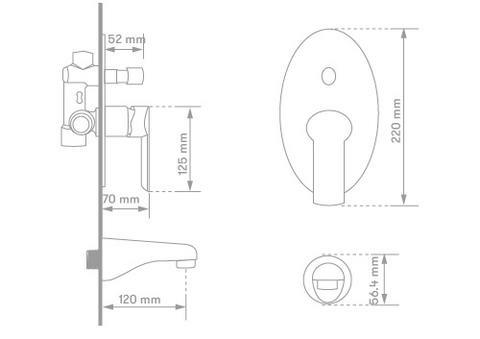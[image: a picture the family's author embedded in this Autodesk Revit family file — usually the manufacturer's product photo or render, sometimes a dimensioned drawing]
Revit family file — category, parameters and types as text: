
# Revit family: 01-3300-11SR-DUCHA KURVEN CON DESVIADOR SIN REGADERA
name_source: partatom
category: Aparatos sanitarios
revit_build: Autodesk Revit 2018 (Build: 20170223_1515(x64)
units: mm (PartAtom-declared; Revit-internal decimal feet)

## family parameters
Anfitrión = Cara
Compartido = No
Corte con vacíos al cargar = No
Cota de conector redondo = Diámetro de uso
Número OmniClass = 23.31.11.00
Punto de cálculo de habitación = No
Tipo de pieza = Normal

## types (1)
- 01-3300-11SR
    Alto = 220 mm  [stored 0.721785 ft]
    Ancho = 130 mm
    Conexión AC = Sí
    Conexión AF = Sí
    Conexión de residuos = No
    Conexión de ventilación = No
    Descripción = DUCHA MONOMANDO
    Elevación por defecto = 0 mm  [stored 0 ft]
    Fabricante = Gricol
    Finish = <Por categoría>
    Imagen de tipo = <Ninguno>
    Largo = 120 mm
    Link Ficha Tecnica = https://infotecnica.gricol.com
    Modelo = 01-3300-11SR
    Product Name = DUCHA MONOMANDO KURVEN CON
DESVIADOR SIN REGADERA
    URL = https://www.gricol.com

note: [stored X ft] marks values corroborated as IEEE doubles in the binary element streams (Revit-internal decimal feet)

## geometry (parser evidence)
native form markers: Blend x2, Sweep x6
no freeform markers — native parametric forms only
